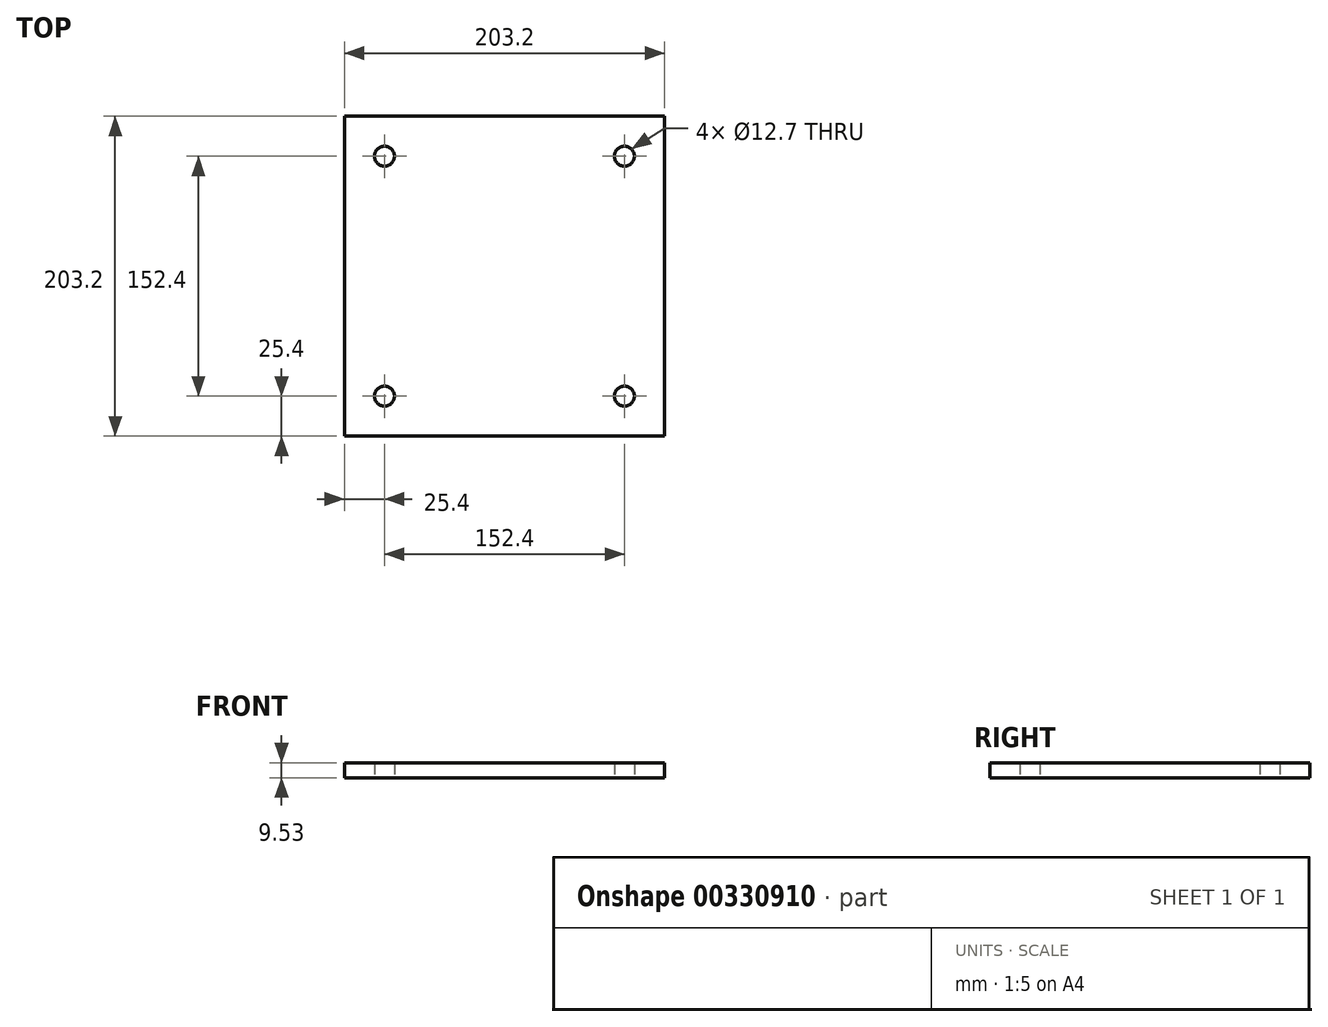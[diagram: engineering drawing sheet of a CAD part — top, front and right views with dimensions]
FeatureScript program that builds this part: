
annotation { "Feature Type Name" : "Feature", "Feature Type Description" : "" }
export const myFeature = defineFeature(function(context is Context, id is Id, definition is map)
    precondition{}
    {
        {
            var Q0;
            Q0=qCreatedBy(makeId("Top.planeOp"),FACE);
            var sketch = newSketch(context, id + "F0", { "sketchPlane" : qUnion([Q0])});
            skLineSegment(sketch, "E0.bottom", {"start": v(101.6, -101.6) * mm, "end": v(-101.6, -101.6) * mm});
            skLineSegment(sketch, "E0.top", {"start": v(101.6, 101.6) * mm, "end": v(-101.6, 101.6) * mm});
            skLineSegment(sketch, "E0.left", {"start": v(101.6, -101.6) * mm, "end": v(101.6, 101.6) * mm});
            skLineSegment(sketch, "E0.right", {"start": v(-101.6, -101.6) * mm, "end": v(-101.6, 101.6) * mm});
            skPoint(sketch, "E0.middle", {"position": v(0, 0) * mm});
            skCircle(sketch, "E1", {"center": v(-76.2, 76.2) * mm, "radius": 6.35 * mm});
            skCircle(sketch, "E2", {"center": v(76.2, 76.2) * mm, "radius": 6.35 * mm});
            skCircle(sketch, "E3", {"center": v(76.2, -76.2) * mm, "radius": 6.35 * mm});
            skCircle(sketch, "E4", {"center": v(-76.2, -76.2) * mm, "radius": 6.35 * mm});
            skSolve(sketch);
        }
        {
            var Q0;
            Q0=makeQuery(id+"F0.imprint","IMPRINT",FACE,{"disambiguationData":[TD([[makeQuery(id+"F0.imprint","IMPRINT",EDGE,{"derivedFrom":sQuery(id+"F0.wireOp",EDGE,"E0.bottom")}),-1.0]])]});
            extrude(context, id + "F1", {"entities" : qUnion([Q0]), "depth" : 9.52 * mm});
        }
    });
